# Revit family: LR1748
name_source: partatom
category: Plumbing Fixtures
revit_build: Autodesk Revit MEP 2016 (Build: 20150220_1215(x64)
units: mm (PartAtom-declared; Revit-internal decimal feet)

## family parameters
Cut with Voids When Loaded = No
Host = Face
OmniClass Number = 23.45.05.14.17
OmniClass Title = Showers
Part Type = Normal
Room Calculation Point = No
Round Connector Dimension = Use Diameter
Shared = Yes

## types (1)
- LR1748
    -EG Enviro-Glaze (Specify Color) = No
    -F Flow Control   2.0GPM (No Longer Available in California) = No
    -LRD Less Recessed Soap Dish = No
    -TF Transformer, 120VAC to 24VAC (-MVC option only) = No
    BRS - Brass Body Valve = No
    CW Connection = Yes
    CWFU = 0.5
    Default Elevation = 63"
    Description = Ligature Resistant Wall Shower ADA Compliant
    HW Connection = Yes
    HWFU = 0.5
    LR1748 - Ligature Resistant Wall Shower = Yes
    MT - Metal Template (Only 1 required Per Project) = No
    MV - Metering Valve, Air-Control Metering = No
    MV-EVS1 - Metering Valve, Electronic Valve System = No
    MV-MTP1 - Metering Valve, Electronic Valve System PLUS = No
    MV-MVC1 - Metering Valve, Time-Trol = No
    MV-PPZ1 - Metering Valve, Programmable Piezo Button = No
    Manufacturer = Acorn Engineering Company
    Material = Stainless Steel-Acorn-Type 304-Satin
    Model = LR1748ADA
    Revised Date = 06/05/2019
    SW - Wall Sleeve = No
    URL = http://www.acorneng.com
    Vent Connection = No
    WFU = 0
    Waste Connection = No

## geometry (parser evidence)
native form markers: Sweep x19
no freeform markers — native parametric forms only
